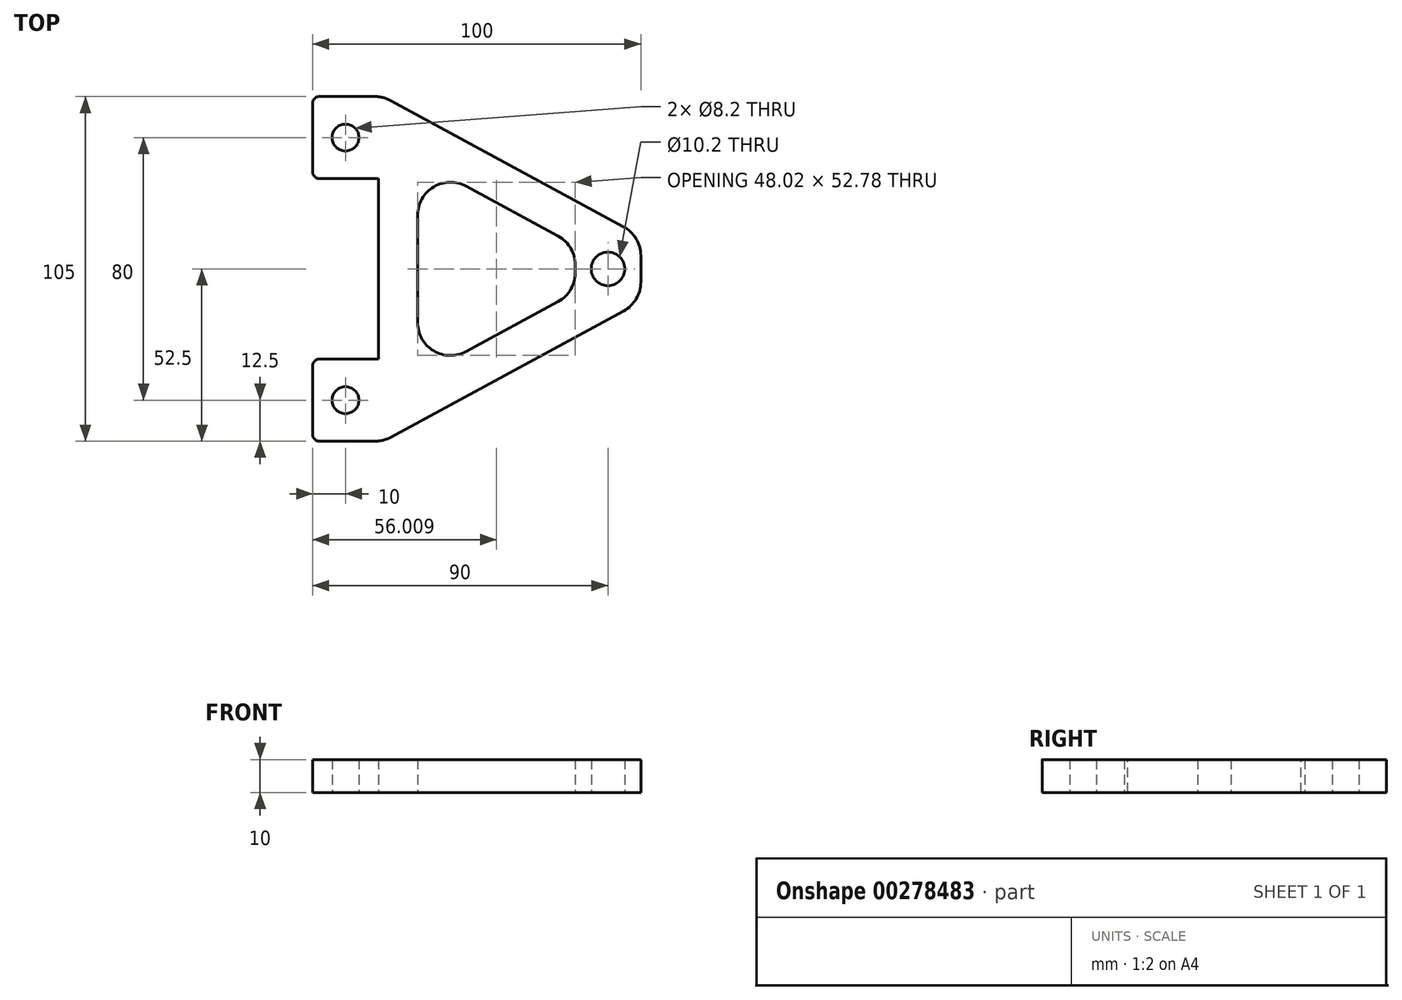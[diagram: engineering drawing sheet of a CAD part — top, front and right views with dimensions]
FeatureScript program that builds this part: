
annotation { "Feature Type Name" : "Feature", "Feature Type Description" : "" }
export const myFeature = defineFeature(function(context is Context, id is Id, definition is map)
    precondition{}
    {
        {
            var Q0;
            Q0=qCreatedBy(makeId("Top.planeOp"),FACE);
            var sketch = newSketch(context, id + "F0", { "sketchPlane" : qUnion([Q0])});
            skCircle(sketch, "E0", {"center": v(-20, 0) * mm, "radius": 4.1 * mm});
            skCircle(sketch, "E1", {"center": v(-20, 80) * mm, "radius": 4.1 * mm});
            skLineSegment(sketch, "E2", {"start": v(-20, 0) * mm, "end": v(-20, 80) * mm, "construction": true});
            skPoint(sketch, "E3", {"position": v(-20, 40) * mm});
            skPoint(sketch, "E4", {"position": v(60, 40) * mm});
            skCircle(sketch, "E5", {"center": v(60, 40) * mm, "radius": 5.1 * mm});
            skLineSegment(sketch, "E6", {"start": v(-30, 92.5) * mm, "end": v(-30, 67.5) * mm});
            skLineSegment(sketch, "E7", {"start": v(-30, 67.5) * mm, "end": v(-10, 67.5) * mm});
            skLineSegment(sketch, "E8", {"start": v(-10, 67.5) * mm, "end": v(-10, 12.5) * mm});
            skLineSegment(sketch, "E9", {"start": v(-10, 12.5) * mm, "end": v(-30, 12.5) * mm});
            skLineSegment(sketch, "E10", {"start": v(-30, 12.5) * mm, "end": v(-30, -12.5) * mm});
            skLineSegment(sketch, "E11", {"start": v(-30, -12.5) * mm, "end": v(-8.48, -12.5) * mm});
            skLineSegment(sketch, "E12", {"start": v(-8.48, -12.5) * mm, "end": v(70, 30) * mm});
            skLineSegment(sketch, "E13", {"start": v(70, 30) * mm, "end": v(70, 50) * mm});
            skLineSegment(sketch, "E14", {"start": v(70, 50) * mm, "end": v(-8.48, 92.5) * mm});
            skLineSegment(sketch, "E15", {"start": v(-8.48, 92.5) * mm, "end": v(-30, 92.5) * mm});
            skLineSegment(sketch, "E16", {"start": v(2, 73.18) * mm, "end": v(2, 6.82) * mm});
            skLineSegment(sketch, "E17", {"start": v(2, 6.82) * mm, "end": v(63.27, 40) * mm});
            skLineSegment(sketch, "E18", {"start": v(63.27, 40) * mm, "end": v(2, 73.18) * mm});
            skLineSegment(sketch, "E19", {"start": v(-20, 40) * mm, "end": v(93.17, 40) * mm, "construction": true});
            skCircle(sketch, "E20", {"center": v(60, 40) * mm, "radius": 10 * mm});
            skSolve(sketch);
        }
        {
            var Q0;
            Q0=makeQuery(id+"F0.imprint","IMPRINT",FACE,{"disambiguationData":[TD([[makeQuery(id+"F0.imprint","IMPRINT",EDGE,{"derivedFrom":sQuery(id+"F0.wireOp",EDGE,"E0")}),-1.0]])]});
            var Q1;
            {var subQ0=sQuery(id+"F0.wireOp",EDGE,"E18");var subQ3=sQuery(id+"F0.wireOp",EDGE,"E5");var subQ9=makeQuery(id+"F0.imprint","INTERSECT",VERTEX,{"disambiguationData":[OD(0.0)],"derivedFrom":[subQ3,subQ0]});Q1=makeQuery(id+"F0.imprint","IMPRINT",FACE,{"disambiguationData":[TD([[makeQuery(id+"F0.imprint","IMPRINT",EDGE,{"disambiguationData":[TD([[subQ9,1.0]])],"derivedFrom":subQ3}),-1.0]])]});}
            var Q2;
            {var subQ0=sQuery(id+"F0.wireOp",EDGE,"E18");var subQ1=sQuery(id+"F0.wireOp",EDGE,"E5");var subQ2=makeQuery(id+"F0.imprint","INTERSECT",VERTEX,{"disambiguationData":[OD(1.0)],"derivedFrom":[subQ1,subQ0]});Q2=makeQuery(id+"F0.imprint","IMPRINT",FACE,{"disambiguationData":[TD([[makeQuery(id+"F0.imprint","IMPRINT",EDGE,{"disambiguationData":[TD([[subQ2,1.0]])],"derivedFrom":subQ1}),-1.0]])]});}
            var Q3;
            {var subQ0=sQuery(id+"F0.wireOp",EDGE,"E18");var subQ1=sQuery(id+"F0.wireOp",EDGE,"E5");var subQ2=makeQuery(id+"F0.imprint","INTERSECT",VERTEX,{"disambiguationData":[OD(0.0)],"derivedFrom":[subQ1,subQ0]});Q3=makeQuery(id+"F0.imprint","IMPRINT",FACE,{"disambiguationData":[TD([[makeQuery(id+"F0.imprint","IMPRINT",EDGE,{"disambiguationData":[TD([[subQ2,-1.0]])],"derivedFrom":subQ1}),-1.0]])]});}
            extrude(context, id + "F1", {"entities" : qUnion([Q0, Q1, Q2, Q3]), "depth" : 10 * mm});
        }
        {
            var Q0;
            Q0=makeQuery(id+"F1.opExtrude","SWEPT_EDGE",EDGE,{"disambiguationData":[OSD([sQuery(id+"F0.wireOp",EDGE,"E14"),sQuery(id+"F0.wireOp",EDGE,"E15")])]});
            var Q1;
            Q1=makeQuery(id+"F1.opExtrude","SWEPT_EDGE",EDGE,{"disambiguationData":[OSD([sQuery(id+"F0.wireOp",EDGE,"E11"),sQuery(id+"F0.wireOp",EDGE,"E12")])]});
            var Q2;
            Q2=makeQuery(id+"F1.opExtrude","SWEPT_EDGE",EDGE,{"disambiguationData":[OSD([sQuery(id+"F0.wireOp",EDGE,"E12"),sQuery(id+"F0.wireOp",EDGE,"E13")])]});
            var Q3;
            Q3=makeQuery(id+"F1.opExtrude","SWEPT_EDGE",EDGE,{"disambiguationData":[OSD([sQuery(id+"F0.wireOp",EDGE,"E13"),sQuery(id+"F0.wireOp",EDGE,"E14")])]});
            var Q4;
            Q4=makeQuery(id+"F1.opExtrude","SWEPT_EDGE",EDGE,{"disambiguationData":[OSD([sQuery(id+"F0.wireOp",EDGE,"E18"),sQuery(id+"F0.wireOp",EDGE,"E20")])]});
            var Q5;
            Q5=makeQuery(id+"F1.opExtrude","SWEPT_EDGE",EDGE,{"disambiguationData":[OSD([sQuery(id+"F0.wireOp",EDGE,"E17"),sQuery(id+"F0.wireOp",EDGE,"E20")])]});
            var Q6;
            Q6=makeQuery(id+"F1.opExtrude","SWEPT_EDGE",EDGE,{"disambiguationData":[OSD([sQuery(id+"F0.wireOp",EDGE,"E16"),sQuery(id+"F0.wireOp",EDGE,"E17")])]});
            var Q7;
            Q7=makeQuery(id+"F1.opExtrude","SWEPT_EDGE",EDGE,{"disambiguationData":[OSD([sQuery(id+"F0.wireOp",EDGE,"E16"),sQuery(id+"F0.wireOp",EDGE,"E18")])]});
            fillet(context, id + "F2", {"entities" : qUnion([Q0, Q1, Q2, Q3, Q4, Q5, Q6, Q7]), "radius" : 10 * mm, "tangentPropagation" : true, "allowEdgeOverflow" : false});
        }
        {
            var Q0;
            Q0=makeQuery(id+"F1.opExtrude","SWEPT_EDGE",EDGE,{"disambiguationData":[OSD([sQuery(id+"F0.wireOp",EDGE,"E6"),sQuery(id+"F0.wireOp",EDGE,"E15")])]});
            var Q1;
            Q1=makeQuery(id+"F1.opExtrude","SWEPT_EDGE",EDGE,{"disambiguationData":[OSD([sQuery(id+"F0.wireOp",EDGE,"E6"),sQuery(id+"F0.wireOp",EDGE,"E7")])]});
            var Q2;
            Q2=makeQuery(id+"F1.opExtrude","SWEPT_EDGE",EDGE,{"disambiguationData":[OSD([sQuery(id+"F0.wireOp",EDGE,"E9"),sQuery(id+"F0.wireOp",EDGE,"E10")])]});
            var Q3;
            Q3=makeQuery(id+"F1.opExtrude","SWEPT_EDGE",EDGE,{"disambiguationData":[OSD([sQuery(id+"F0.wireOp",EDGE,"E10"),sQuery(id+"F0.wireOp",EDGE,"E11")])]});
            fillet(context, id + "F3", {"entities" : qUnion([Q0, Q1, Q2, Q3]), "radius" : 2 * mm, "tangentPropagation" : true, "allowEdgeOverflow" : false});
        }
    });
